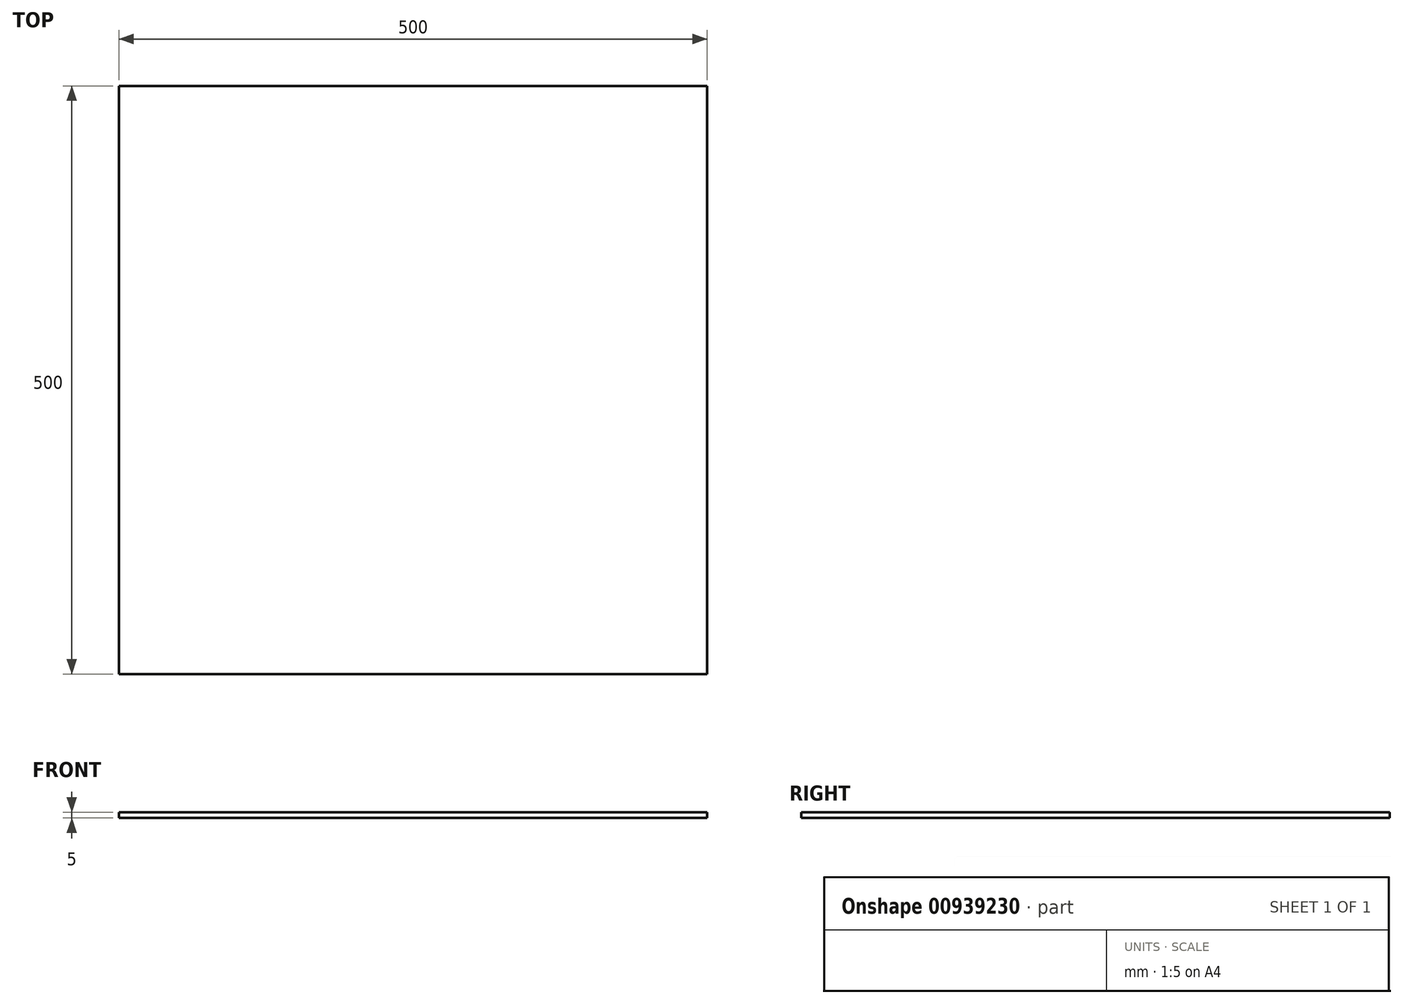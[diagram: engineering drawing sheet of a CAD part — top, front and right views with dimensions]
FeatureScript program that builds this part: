
annotation { "Feature Type Name" : "Feature", "Feature Type Description" : "" }
export const myFeature = defineFeature(function(context is Context, id is Id, definition is map)
    precondition{}
    {
        {
            var Q0;
            Q0=qCreatedBy(makeId("Top.planeOp"),FACE);
            var sketch = newSketch(context, id + "F0", { "sketchPlane" : qUnion([Q0])});
            skLineSegment(sketch, "E0.bottom", {"start": v(250, -250) * mm, "end": v(-250, -250) * mm});
            skLineSegment(sketch, "E0.top", {"start": v(250, 250) * mm, "end": v(-250, 250) * mm});
            skLineSegment(sketch, "E0.left", {"start": v(250, -250) * mm, "end": v(250, 250) * mm});
            skLineSegment(sketch, "E0.right", {"start": v(-250, -250) * mm, "end": v(-250, 250) * mm});
            skPoint(sketch, "E0.middle", {"position": v(0, 0) * mm});
            skSolve(sketch);
        }
        {
            var Q0;
            Q0=makeQuery(id+"F0.imprint","IMPRINT",FACE,{"disambiguationData":[TD([[makeQuery(id+"F0.imprint","IMPRINT",EDGE,{"derivedFrom":sQuery(id+"F0.wireOp",EDGE,"E0.bottom")}),-1.0]])]});
            extrude(context, id + "F1", {"entities" : qUnion([Q0]), "oppositeDirection" : true, "depth" : 5 * mm, "offsetDistance" : 25 * mm});
        }
    });
